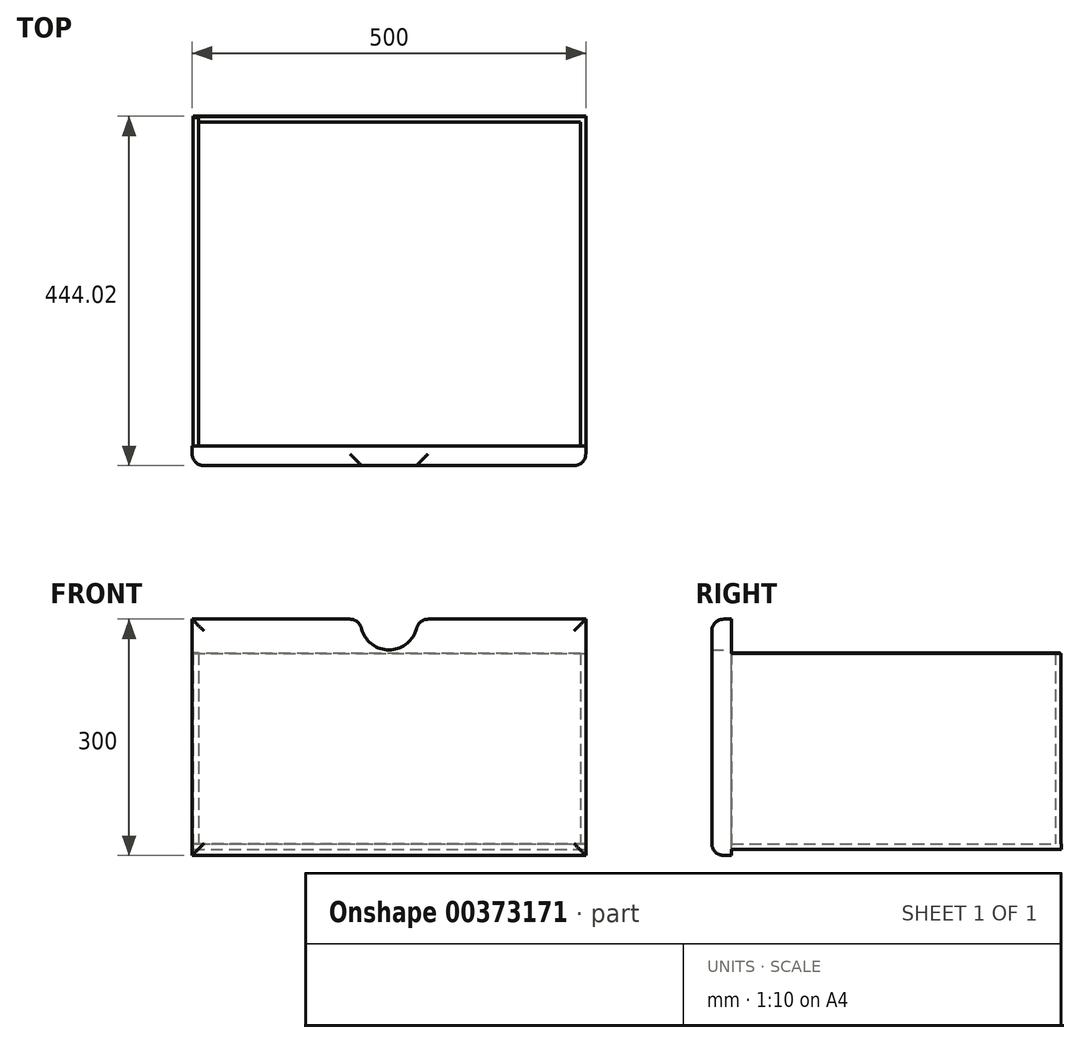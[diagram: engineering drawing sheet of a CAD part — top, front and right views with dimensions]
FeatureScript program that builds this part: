
annotation { "Feature Type Name" : "Feature", "Feature Type Description" : "" }
export const myFeature = defineFeature(function(context is Context, id is Id, definition is map)
    precondition{}
    {
        {
            var Q0;
            Q0=qCreatedBy(makeId("Front.planeOp"),FACE);
            var sketch = newSketch(context, id + "F0", { "sketchPlane" : qUnion([Q0])});
            skLineSegment(sketch, "E0.bottom", {"start": v(250, -150) * mm, "end": v(-250, -150) * mm});
            skLineSegment(sketch, "E0.top", {"start": v(250, 150) * mm, "end": v(-250, 150) * mm});
            skLineSegment(sketch, "E0.left", {"start": v(250, -150) * mm, "end": v(250, 150) * mm});
            skLineSegment(sketch, "E0.right", {"start": v(-250, -150) * mm, "end": v(-250, 150) * mm});
            skPoint(sketch, "E0.middle", {"position": v(0, 0) * mm});
            skSolve(sketch);
        }
        {
            var Q0;
            Q0=makeQuery(id+"F0.imprint","IMPRINT",FACE,{"disambiguationData":[TD([[makeQuery(id+"F0.imprint","IMPRINT",EDGE,{"derivedFrom":sQuery(id+"F0.wireOp",EDGE,"E0.bottom")}),-1.0]])]});
            var sketch = newSketch(context, id + "F1", { "sketchPlane" : qUnion([Q0])});
            skSolve(sketch);
        }
        {
            var Q0;
            Q0=makeQuery(id+"F0.imprint","IMPRINT",FACE,{"disambiguationData":[TD([[makeQuery(id+"F0.imprint","IMPRINT",EDGE,{"derivedFrom":sQuery(id+"F0.wireOp",EDGE,"E0.bottom")}),-1.0]])]});
            var sketch = newSketch(context, id + "F2", { "sketchPlane" : qUnion([Q0])});
            skCircle(sketch, "E1", {"center": v(0, 147.27) * mm, "radius": 36.18 * mm});
            skSolve(sketch);
        }
        {
            var Q0;
            Q0=makeQuery(id+"F0.imprint","IMPRINT",FACE,{"disambiguationData":[TD([[makeQuery(id+"F0.imprint","IMPRINT",EDGE,{"derivedFrom":sQuery(id+"F0.wireOp",EDGE,"E0.bottom")}),-1.0]])]});
            extrude(context, id + "F3", {"entities" : qUnion([Q0]), "depth" : 25 * mm});
        }
        {
            var Q0;
            Q0=makeQuery(id+"F3.opExtrude","SWEPT_FACE",FACE,{"disambiguationData":[OSD([sQuery(id+"F0.wireOp",EDGE,"E0.left")])]});
            var sketch = newSketch(context, id + "F4", { "sketchPlane" : qUnion([Q0])});
            skLineSegment(sketch, "E2.bottom", {"start": v(-25, 106.58) * mm, "end": v(418.72, 106.58) * mm});
            skLineSegment(sketch, "E2.top", {"start": v(-25, -142.54) * mm, "end": v(418.72, -142.54) * mm});
            skLineSegment(sketch, "E2.left", {"start": v(-25, 106.58) * mm, "end": v(-25, -142.54) * mm});
            skLineSegment(sketch, "E2.right", {"start": v(418.72, 106.58) * mm, "end": v(418.72, -142.54) * mm});
            skSolve(sketch);
        }
        {
            var Q0;
            {var subQ0=sQuery(id+"F4.wireOp",EDGE,"E2.right");Q0=makeQuery(id+"F4.imprint","IMPRINT",FACE,{"disambiguationData":[TD([[makeQuery(id+"F4.imprint","IMPRINT",EDGE,{"derivedFrom":subQ0}),-1.0]])]});}
            extrude(context, id + "F5", {"entities" : qUnion([Q0]), "operationType" : NewBodyOperationType.ADD, "oppositeDirection" : true, "depth" : 7 * mm});
        }
        {
            var Q0;
            Q0=makeQuery(id+"F5.opExtrude","SWEPT_FACE",FACE,{"disambiguationData":[OSD([sQuery(id+"F4.wireOp",EDGE,"E2.top")])]});
            var sketch = newSketch(context, id + "F6", { "sketchPlane" : qUnion([Q0])});
            skLineSegment(sketch, "E3.bottom", {"start": v(250, 0) * mm, "end": v(-249.12, 0) * mm});
            skLineSegment(sketch, "E3.top", {"start": v(250, -419.02) * mm, "end": v(-249.12, -419.02) * mm});
            skLineSegment(sketch, "E3.left", {"start": v(250, 0) * mm, "end": v(250, -419.02) * mm});
            skLineSegment(sketch, "E3.right", {"start": v(-249.12, 0) * mm, "end": v(-249.12, -419.02) * mm});
            skSolve(sketch);
        }
        {
            var Q0;
            {var subQ3=sQuery(id+"F6.wireOp",EDGE,"E3.top");Q0=makeQuery(id+"F6.imprint","IMPRINT",FACE,{"disambiguationData":[TD([[makeQuery(id+"F6.imprint","IMPRINT",EDGE,{"derivedFrom":subQ3}),-1.0]])]});}
            extrude(context, id + "F7", {"entities" : qUnion([Q0]), "operationType" : NewBodyOperationType.ADD, "oppositeDirection" : true, "depth" : 7 * mm});
        }
        {
            var Q0;
            Q0=makeQuery(id+"F7.opExtrude","SWEPT_FACE",FACE,{"disambiguationData":[OSD([sQuery(id+"F6.wireOp",EDGE,"E3.right")])]});
            var sketch = newSketch(context, id + "F8", { "sketchPlane" : qUnion([Q0])});
            skPoint(sketch, "E4.oppositeSnap0", {"position": v(-419.02, -139.04) * mm});
            skLineSegment(sketch, "E4.bottom", {"start": v(22.34, 107.28) * mm, "end": v(-417.42, 107.28) * mm});
            skLineSegment(sketch, "E4.top", {"start": v(22.34, -139.04) * mm, "end": v(-417.42, -139.04) * mm});
            skLineSegment(sketch, "E4.left", {"start": v(22.34, 107.28) * mm, "end": v(22.34, -139.04) * mm});
            skLineSegment(sketch, "E4.right", {"start": v(-417.42, 107.28) * mm, "end": v(-417.42, -139.04) * mm});
            skSolve(sketch);
        }
        {
            var Q0;
            {var subQ1=sQuery(id+"F8.wireOp",EDGE,"E4.bottom");Q0=makeQuery(id+"F8.imprint","IMPRINT",FACE,{"disambiguationData":[TD([[makeQuery(id+"F8.imprint","IMPRINT",EDGE,{"derivedFrom":subQ1}),1.0]])]});}
            extrude(context, id + "F9", {"entities" : qUnion([Q0]), "operationType" : NewBodyOperationType.ADD, "oppositeDirection" : true, "depth" : 7 * mm});
        }
        {
            var Q0;
            Q0=makeQuery(id+"F5.opExtrude","SWEPT_FACE",FACE,{"disambiguationData":[OSD([sQuery(id+"F4.wireOp",EDGE,"E2.right")])]});
            var sketch = newSketch(context, id + "F10", { "sketchPlane" : qUnion([Q0])});
            skLineSegment(sketch, "E5.bottom", {"start": v(-250, 106.58) * mm, "end": v(248.88, 106.58) * mm});
            skLineSegment(sketch, "E5.top", {"start": v(-250, -140.4) * mm, "end": v(248.88, -140.4) * mm});
            skLineSegment(sketch, "E5.left", {"start": v(-250, 106.58) * mm, "end": v(-250, -140.4) * mm});
            skLineSegment(sketch, "E5.right", {"start": v(248.88, 106.58) * mm, "end": v(248.88, -140.4) * mm});
            skSolve(sketch);
        }
        {
            var Q0;
            {var subQ3=sQuery(id+"F10.wireOp",EDGE,"E5.top");Q0=makeQuery(id+"F10.imprint","IMPRINT",FACE,{"disambiguationData":[TD([[makeQuery(id+"F10.imprint","IMPRINT",EDGE,{"derivedFrom":subQ3}),1.0]])]});}
            extrude(context, id + "F11", {"entities" : qUnion([Q0]), "operationType" : NewBodyOperationType.ADD, "oppositeDirection" : true, "depth" : 7 * mm});
        }
        {
            var Q0;
            Q0=sQuery(id+"F2.wireOp",EDGE,"E1");
            extrude(context, id + "F12", {"bodyType" : ToolBodyType.SURFACE, "surfaceEntities" : qUnion([Q0]), "depth" : 8 * mm});
        }
        {
            var Q0;
            Q0 = qSketchRegion(id + "F2", true);
            var Q1;
            Q1=sQuery(id+"F2.wireOp",EDGE,"E1");
            extrude(context, id + "F13", {"entities" : qUnion([Q0]), "operationType" : NewBodyOperationType.REMOVE, "surfaceEntities" : qUnion([Q1]), "depth" : 25 * mm, "hasSecondDirection" : true, "secondDirectionBound" : SecondDirectionBoundingType.THROUGH_ALL, "secondDirectionOppositeDirection" : true, "secondDirectionDepth" : 25 * mm});
        }
        {
            var Q0;
            Q0=makeQuery(id+"F12.opExtrude","SWEPT_BODY",BODY,{"disambiguationData":[OSD([sQuery(id+"F2.wireOp",EDGE,"E1")])]});
            deleteBodies(context, id + "F14", {"entities" : qUnion([Q0])});
        }
        {
            var Q0;
            Q0=makeQuery(id+"F13.boolean.opBoolean","INTERSECT",EDGE,{"disambiguationData":[OD(1.0)],"derivedFrom":[makeQuery(id+"F3.opExtrude","SWEPT_FACE",FACE,{"disambiguationData":[OSD([sQuery(id+"F0.wireOp",EDGE,"E0.top")])]}),makeQuery(id+"F13.opExtrude","SWEPT_FACE",FACE,{"disambiguationData":[OSD([sQuery(id+"F2.wireOp",EDGE,"E1")])]})]});
            var Q1;
            Q1=makeQuery(id+"F13.boolean.opBoolean","INTERSECT",EDGE,{"disambiguationData":[OD(0.0)],"derivedFrom":[makeQuery(id+"F3.opExtrude","SWEPT_FACE",FACE,{"disambiguationData":[OSD([sQuery(id+"F0.wireOp",EDGE,"E0.top")])]}),makeQuery(id+"F13.opExtrude","SWEPT_FACE",FACE,{"disambiguationData":[OSD([sQuery(id+"F2.wireOp",EDGE,"E1")])]})]});
            var Q2;
            {var subQ0=sQuery(id+"F0.wireOp",EDGE,"E0.left");var subQ1=sQuery(id+"F0.wireOp",EDGE,"E0.top");Q2=makeQuery(id+"F13.boolean.opBoolean","SPLIT",EDGE,{"disambiguationData":[TD([makeQuery(id+"F3.opExtrude","SWEPT_FACE",FACE,{"disambiguationData":[OSD([subQ0])]})])],"derivedFrom":makeQuery(id+"F3.opExtrude","CAP_EDGE",EDGE,{"disambiguationData":[OSD([subQ1])],"isStart":false})});}
            var Q3;
            {var subQ0=sQuery(id+"F0.wireOp",EDGE,"E0.right");var subQ1=sQuery(id+"F0.wireOp",EDGE,"E0.top");Q3=makeQuery(id+"F13.boolean.opBoolean","SPLIT",EDGE,{"disambiguationData":[TD([makeQuery(id+"F3.opExtrude","SWEPT_FACE",FACE,{"disambiguationData":[OSD([subQ0])]})])],"derivedFrom":makeQuery(id+"F3.opExtrude","CAP_EDGE",EDGE,{"disambiguationData":[OSD([subQ1])],"isStart":false})});}
            var Q4;
            Q4=makeQuery(id+"F3.opExtrude","CAP_EDGE",EDGE,{"disambiguationData":[OSD([sQuery(id+"F0.wireOp",EDGE,"E0.right")])],"isStart":false});
            var Q5;
            Q5=makeQuery(id+"F3.opExtrude","CAP_EDGE",EDGE,{"disambiguationData":[OSD([sQuery(id+"F0.wireOp",EDGE,"E0.bottom")])],"isStart":false});
            var Q6;
            Q6=makeQuery(id+"F3.opExtrude","CAP_EDGE",EDGE,{"disambiguationData":[OSD([sQuery(id+"F0.wireOp",EDGE,"E0.left")])],"isStart":false});
            fillet(context, id + "F15", {"entities" : qUnion([Q0, Q1, Q2, Q3, Q4, Q5, Q6]), "radius" : 15 * mm, "tangentPropagation" : true, "allowEdgeOverflow" : false});
        }
        {
            var Q0;
            Q0=makeQuery(id+"F3.opExtrude","SWEPT_BODY",BODY,{"disambiguationData":[OSD([sQuery(id+"F0.wireOp",EDGE,"E0.bottom"),sQuery(id+"F0.wireOp",EDGE,"E0.top"),sQuery(id+"F0.wireOp",EDGE,"E0.left"),sQuery(id+"F0.wireOp",EDGE,"E0.right")])]});
            transform(context, id + "F16", {"entities" : qUnion([Q0]), "transformType" : TransformType.TRANSLATION_3D, "dx" : 0 * mm, "dy" : 0 * mm, "dz" : 0 * mm, "makeCopy" : true});
        }
    });
